# Revit family: NLRS_00_AIR_Muurrooster_ST-431-RC2_Storax
name_source: partatom
category: Air Terminals
units: mm (PartAtom-declared; Revit-internal decimal feet)

## family parameters
Cut with Voids When Loaded = No
Host = Face
Part Type = Normal
Room Calculation Point = Yes
Round Connector Dimension = Use Diameter
Shared = No

## types (1)
- ST-431-RC2
    Apparent Load = 0 VA
    Assembly Code = 57.10.90.1
    Based On = Renson
    Default Elevation = 1219 mm
    Description = ST-431-RC2
    Export Type to IFC As = IfcAirTerminalType
    IfcExportAs = IfcAirTerminalType
    IfcExportType = Grille
    Manufacturer = Storax
    Model = ST-431-RC2
    RSen_C_code_CBNL = Louvre
    RSen_C_code_ETIM = Overstroomrooster
    RSen_C_code_ETIM_URL = https://www.storax.nl
    RSen_C_code_article = ST-431-RC2
    RSen_C_code_gtin = -
    RSen_C_content_provider = Storax
    RSen_C_depth = 29 mm  [stored 0.0951444 ft]
    RSen_C_description = ST-431-RC2
    RSen_C_material = RSen_h4_aluminum
    RSen_C_model = ST-431-RC2
    RSen_C_type = surface-mounted wall louvre
    RSen_C_type_comments = surface-mounted wall louvre
    STX_I BaseKeynote = 57.10.90.1
    STX_I Blade_pitch = 33 mm
    STX_I Blade_shape = Z
    STX_I Blade_type = L.033.01
    STX_I Burglarproof_WK class = -
    STX_I Cd coefficient_discharge = 0.226
    STX_I Ce coefficient_intake = 0.221
    STX_I Control = -
    STX_I Depth_max = 0 mm  [stored 0 ft]
    STX_I Depth_min = 0 mm  [stored 0 ft]
    STX_I Drainage profile = No
    STX_I Fire resistance = -
    STX_I Flange_height = 0 mm  [stored 0 ft]
    STX_I Flange_thickness = 0 mm  [stored 0 ft]
    STX_I Flange_width = 0 mm  [stored 0 ft]
    STX_I G4 filter = No
    STX_I Height_max = 4000 mm  [stored 13.1234 ft]
    STX_I Height_min = 120 mm  [stored 0.393701 ft]
    STX_I IP = IP2XD
    STX_I K factor_discharge = 19.58
    STX_I K factor_intake = 20.47
    STX_I Material = aluminiumAlMgSi0.5
    STX_I Puncture proof = Yes
    STX_I Removable insect mesh_info = Min. dimensions: 190x190 mm; Max. dimensions: 1500x1200 mm
    STX_I Shape = rectangular
    STX_I Size_maximum = see price list
    STX_I Sound reduction_Dw = -
    STX_I Sound reduction_Rw = -
    STX_I U-value = -
    STX_I Visual free area = 0.59
    STX_I Water channel = Yes
    STX_I Width_max = 4000 mm  [stored 13.1234 ft]
    STX_I Width_min = 120 mm  [stored 0.393701 ft]
    STX_I Without flange = No
    STX_I Without flange_info = no
    STX_I Zichtbaar vrije opp. = 0.5
    STX_V Air exhaust = No
    STX_V Supply air = Yes
    STX_W Fingerprint = <RSen_C_length> x <RSen_C_height> mm
    Type Comments = surface-mounted wall louvre
    Type IFC Predefined Type = Grille
    ZZZ_Airflow_HVACAirflow = 1.0 m³/h
    ZZZ_Cut out_depth negative_Length = 2 mm  [stored 0.00656168 ft]
    ZZZ_Cut out_depth_Length = 500 mm  [stored 1.64042 ft]
    ZZZ_Depth negative_Length = -29 mm  [stored -0.0951444 ft]
    ZZZ_Depth_Length = 29 mm  [stored 0.0951444 ft]
    ZZZ_Dust filter_FamilyType_Air Terminals = dust filter - class g4 - SH_renson : dust filter - class g4_renson
    ZZZ_Flange_FamilyType_Air Terminals = GEO_flange_renson_431RC2 : standard
    ZZZ_Flange_offset_Length = 14 mm  [stored 0.0459318 ft]
    ZZZ_Flange_thickness_Length = 1 mm  [stored 0.00328084 ft]
    ZZZ_Louvre_insertion point negative_Length = 0 mm  [stored 0 ft]
    ZZZ_Louvre_insertion point_Length = 0 mm  [stored 0 ft]
    ZZZ_Louvre_rotation_Angle = 0.00°
    ZZZ_Profile bottom_minimum height_Length = 23 mm  [stored 0.0754593 ft]
    ZZZ_Profile middle_offset_Length = 33 mm
    ZZZ_Profile top_offset_Length = 51 mm
    ZZZ_Protrusion_Length = 0 mm  [stored 0 ft]
    ZZZ_Recess depth_Length = 0 mm  [stored 0 ft]
    ZZZ_Recess depth_negative_Length = 0 mm  [stored 0 ft]
    ZZZ_Recessed_YesNo = No
    ZZZ_Surface mounted_YesNo = Yes

note: [stored X ft] marks values corroborated as IEEE doubles in the binary element streams (Revit-internal decimal feet)

## geometry (parser evidence)
native form markers: Sweep x74
no freeform markers — native parametric forms only
